# Revit family: ASL_Designline_AL_Door_125mm_Jamb
name_source: partatom
category: Detail Items
revit_build: Autodesk Revit 2018 (Build: 20170223_1515(x64)
units: mm (PartAtom-declared; Revit-internal decimal feet)

## family parameters
Rotate with component = No
Section Shape = Not Defined
Shared = Yes

## types (5) — shared parameters
10mm Plasterboard = No
13mm Plasterboard = Yes
ASL 415 = No
ASL 420 = Yes
Manufacturer = Aluminate Solutions Limited
Masking Region = Yes
Plasterboard Head Parametric = 7 mm  [stored 0.0229659 ft]
Technical Info = www.aluminate.nz

## per-type parameters (varying)
| type | 50mm Door Jamb Standard | 64mm Steel Stud | 92mm Steel Stud | ASL Hinge Stile Hinge Door 100mm | ASL Hinge Stile Hinge Door 125mm | Glazing | Hinge_Single | Timber Frame | Type Comments |
| ASL 420 64 Steel Frame Wall Glazing | No | Yes | No | No | No | Yes | No | No | ASL Designline ASL 420 Jamb With 64mm Steel Stud With Glazing |
| ASL 420 92 Steel Frame Wall Glazing | No | No | Yes | No | No | Yes | No | No | ASL Designline ASL 420 Jamb With 92mm Steel Stud With Glazing |
| ASL 420 92 Steel Frame Wall Single Action ASL Hinge Stile Door Suite 125mm | Yes | No | Yes | Yes | Yes | No | Yes | No | ASL Designline ASL 420 Jamb With 92mm Steel Stud With ASL 100mm Hinge Stile Door Suite |
| ASL 420 64 Steel Frame Wall Single Action ASL Hinge Stile Door Suite 125mm | Yes | Yes | No | Yes | Yes | No | Yes | No | ASL Designline ASL 420 Jamb With 64mm Steel Stud With ASL 100mm Hinge Stile Door Suite |
| ASL 415 Timber Frame Wall Single Action ASL Hinge Stile Door Suite 125mm | Yes | No | No | Yes | Yes | No | Yes | Yes | ASL Designline ASL 415 Jamb With 90mm Timber Stud With ASL 125mm Hinge Stile Door Suite |

note: [stored X ft] marks values corroborated as IEEE doubles in the binary element streams (Revit-internal decimal feet)

## geometry (parser evidence)
native form markers: Sweep x10
no freeform markers — native parametric forms only
